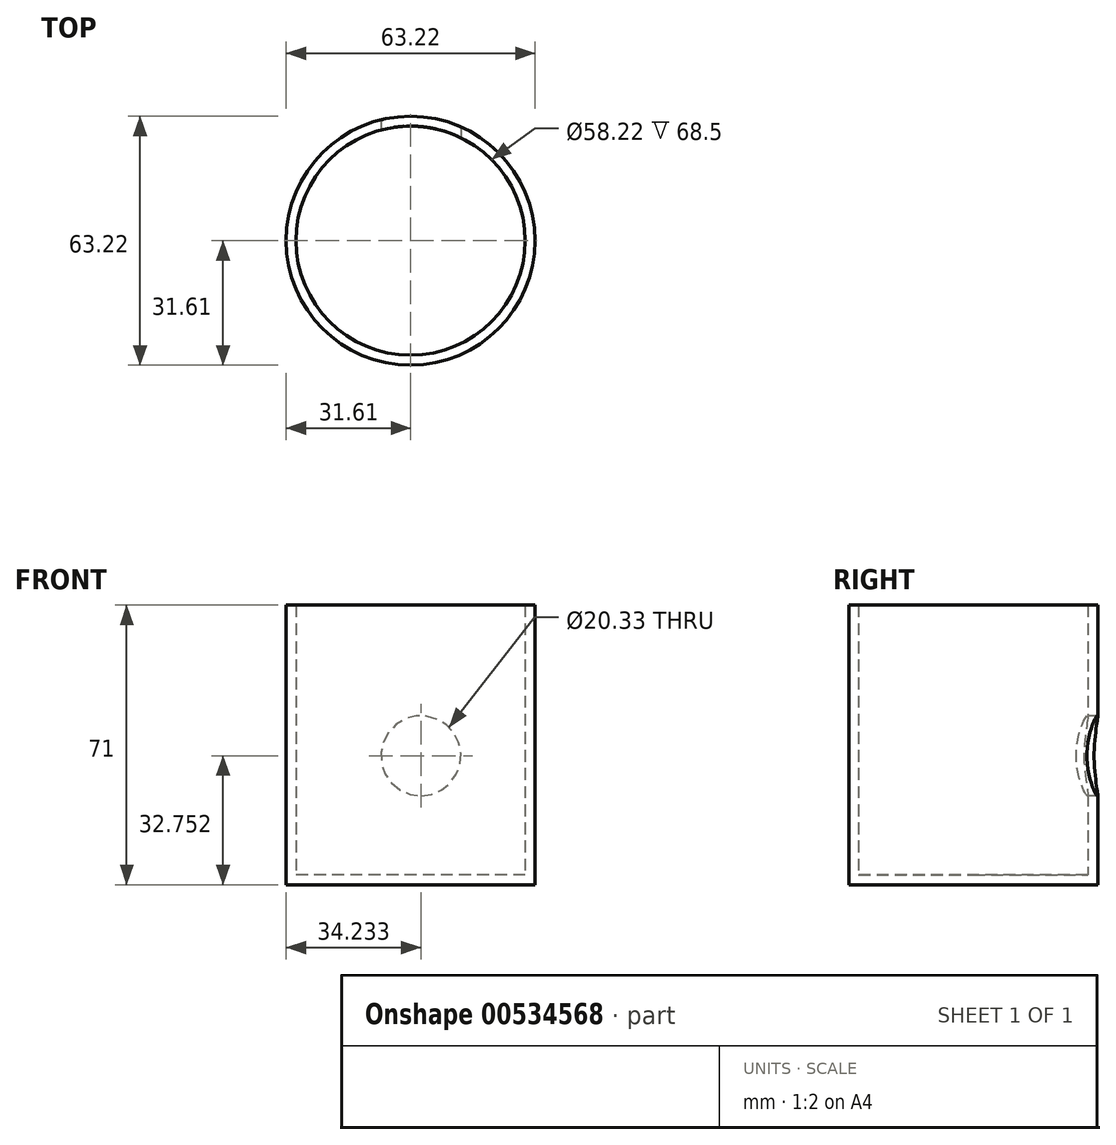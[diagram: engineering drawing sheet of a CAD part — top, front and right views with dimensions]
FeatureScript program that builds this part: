
annotation { "Feature Type Name" : "Feature", "Feature Type Description" : "" }
export const myFeature = defineFeature(function(context is Context, id is Id, definition is map)
    precondition{}
    {
        {
            var Q0;
            Q0=qCreatedBy(makeId("Top.planeOp"),FACE);
            var sketch = newSketch(context, id + "F0", { "sketchPlane" : qUnion([Q0])});
            skCircle(sketch, "E0", {"center": v(0, 0) * mm, "radius": 31.61 * mm});
            skSolve(sketch);
        }
        {
            var Q0;
            Q0=makeQuery(id+"F0.imprint","IMPRINT",FACE,{"disambiguationData":[TD([[makeQuery(id+"F0.imprint","IMPRINT",EDGE,{"derivedFrom":sQuery(id+"F0.wireOp",EDGE,"E0")}),1.0]])]});
            extrude(context, id + "F1", {"entities" : qUnion([Q0]), "depth" : 71 * mm, "offsetDistance" : 25 * mm});
        }
        {
            var Q0;
            Q0=makeQuery(id+"F1.opExtrude","CAP_FACE",FACE,{"disambiguationData":[OSD([sQuery(id+"F0.wireOp",EDGE,"E0")])],"isStart":false});
            shell(context, id + "F2", {"entities" : qUnion([Q0]), "thickness" : 2.5 * mm});
        }
        {
            var Q0;
            Q0=qCreatedBy(makeId("Front.planeOp"),FACE);
            var sketch = newSketch(context, id + "F3", { "sketchPlane" : qUnion([Q0])});
            skCircle(sketch, "E1", {"center": v(2.62, 32.75) * mm, "radius": 10.16 * mm});
            skSolve(sketch);
        }
        {
            var Q0;
            Q0=makeQuery(id+"F3.imprint","IMPRINT",FACE,{"disambiguationData":[TD([[makeQuery(id+"F3.imprint","IMPRINT",EDGE,{"derivedFrom":sQuery(id+"F3.wireOp",EDGE,"E1")}),1.0]])]});
            var Q1;
            Q1=sQuery(id+"F3.wireOp",EDGE,"E1");
            extrude(context, id + "F4", {"entities" : qUnion([Q0]), "operationType" : NewBodyOperationType.REMOVE, "surfaceEntities" : qUnion([Q1]), "oppositeDirection" : true, "depth" : 100 * mm, "offsetDistance" : 25 * mm});
        }
    });
